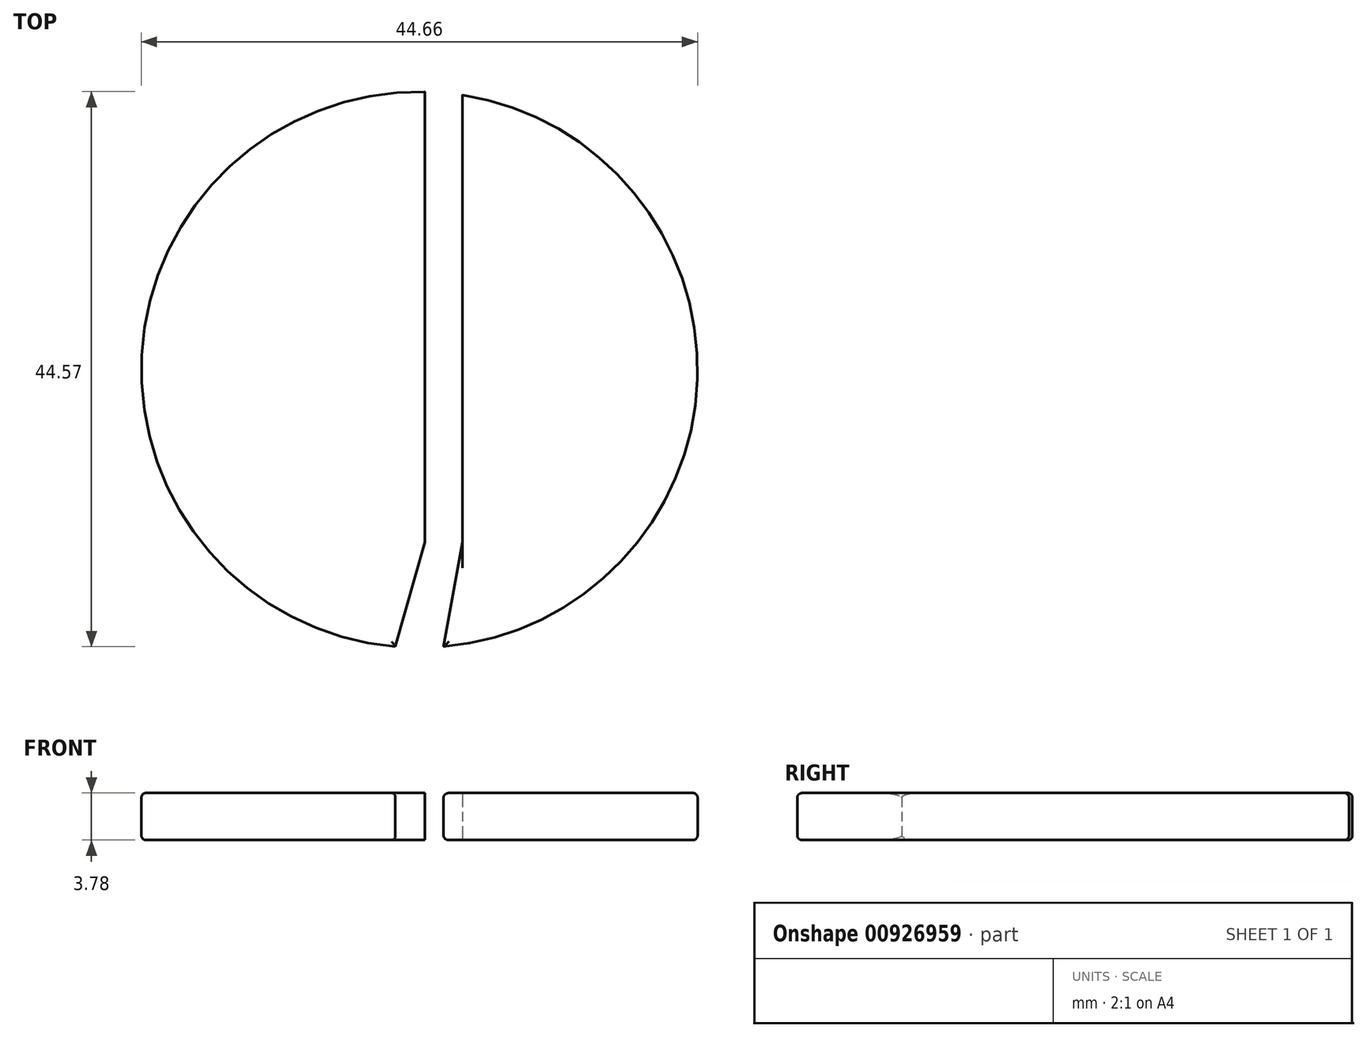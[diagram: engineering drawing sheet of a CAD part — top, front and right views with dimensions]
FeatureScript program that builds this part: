
annotation { "Feature Type Name" : "Feature", "Feature Type Description" : "" }
export const myFeature = defineFeature(function(context is Context, id is Id, definition is map)
    precondition{}
    {
        {
            var Q0;
            Q0=qCreatedBy(makeId("Top.planeOp"),FACE);
            var sketch = newSketch(context, id + "F0", { "sketchPlane" : qUnion([Q0])});
            skArc(sketch, "E0", {"start": v(1.93, -22.24) * mm, "mid": v(0, 22.33) * mm, "end": v(-1.93, -22.24) * mm});
            skLineSegment(sketch, "E1", {"start": v(1.93, -22.24) * mm, "end": v(3.44, -13.85) * mm});
            skLineSegment(sketch, "E2", {"start": v(3.44, -13.85) * mm, "end": v(3.44, 51.54) * mm});
            skLineSegment(sketch, "E3.MirrorCS", {"start": v(0.42, -13.85) * mm, "end": v(0.42, 51.54) * mm});
            skLineSegment(sketch, "E4.MirrorCS", {"start": v(-1.93, -22.24) * mm, "end": v(0.42, -13.85) * mm});
            skArc(sketch, "E5", {"start": v(3.44, 51.54) * mm, "mid": v(1.93, 52.95) * mm, "end": v(0.42, 51.54) * mm});
            skSolve(sketch);
        }
        {
            var Q0;
            Q0=makeQuery(id+"F0.imprint","IMPRINT",FACE,{"disambiguationData":[TD([[makeQuery(id+"F0.imprint","IMPRINT",EDGE,{"derivedFrom":sQuery(id+"F0.wireOp",EDGE,"E0")}),1.0]])]});
            extrude(context, id + "F1", {"entities" : qUnion([Q0]), "depth" : 3.78 * mm, "offsetDistance" : 25.4 * mm});
        }
        {
            var Q0;
            Q0=makeQuery(id+"F1.opExtrude","CAP_EDGE",EDGE,{"disambiguationData":[OSD([sQuery(id+"F0.wireOp",EDGE,"E0")])],"isStart":false});
            var Q1;
            Q1=makeQuery(id+"F1.opExtrude","CAP_EDGE",EDGE,{"disambiguationData":[OSD([sQuery(id+"F0.wireOp",EDGE,"E0")])],"isStart":true});
            var Q2;
            Q2=makeQuery(id+"F1.opExtrude","CAP_EDGE",EDGE,{"disambiguationData":[OSD([sQuery(id+"F0.wireOp",EDGE,"E2")])],"isStart":false});
            var Q3;
            Q3=makeQuery(id+"F1.opExtrude","CAP_EDGE",EDGE,{"disambiguationData":[OSD([sQuery(id+"F0.wireOp",EDGE,"E3.MirrorCS")])],"isStart":false});
            var Q4;
            Q4=makeQuery(id+"F1.opExtrude","CAP_EDGE",EDGE,{"disambiguationData":[OSD([sQuery(id+"F0.wireOp",EDGE,"E1")])],"isStart":false});
            var Q5;
            Q5=makeQuery(id+"F1.opExtrude","CAP_EDGE",EDGE,{"disambiguationData":[OSD([sQuery(id+"F0.wireOp",EDGE,"E4.MirrorCS")])],"isStart":false});
            var Q6;
            Q6=makeQuery(id+"F1.opExtrude","CAP_EDGE",EDGE,{"disambiguationData":[OSD([sQuery(id+"F0.wireOp",EDGE,"E1")])],"isStart":true});
            var Q7;
            Q7=makeQuery(id+"F1.opExtrude","CAP_EDGE",EDGE,{"disambiguationData":[OSD([sQuery(id+"F0.wireOp",EDGE,"E4.MirrorCS")])],"isStart":true});
            var Q8;
            Q8=makeQuery(id+"F1.opExtrude","CAP_EDGE",EDGE,{"disambiguationData":[OSD([sQuery(id+"F0.wireOp",EDGE,"E3.MirrorCS")])],"isStart":true});
            var Q9;
            Q9=makeQuery(id+"F1.opExtrude","CAP_EDGE",EDGE,{"disambiguationData":[OSD([sQuery(id+"F0.wireOp",EDGE,"E2")])],"isStart":true});
            fillet(context, id + "F2", {"entities" : qUnion([Q0, Q1, Q2, Q3, Q4, Q5, Q6, Q7, Q8, Q9]), "radius" : 0.37 * mm, "tangentPropagation" : true, "allowEdgeOverflow" : false});
        }
    });
